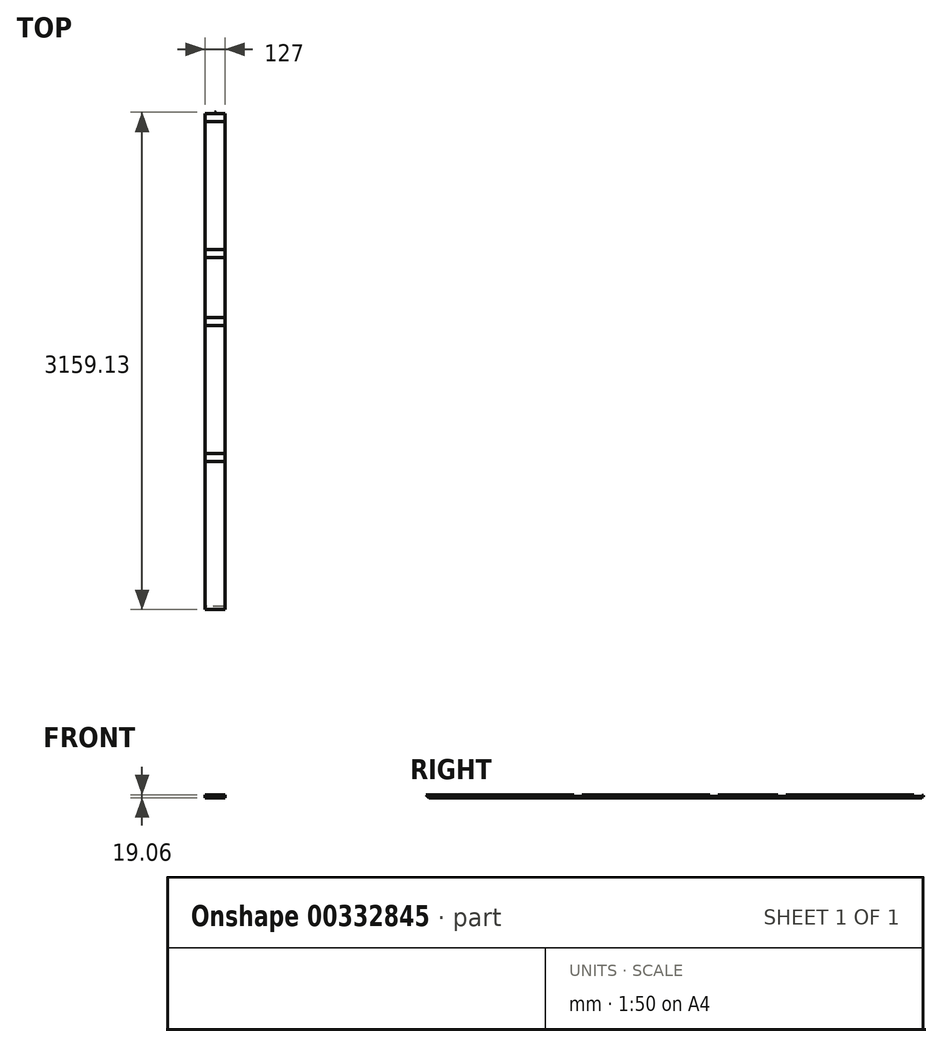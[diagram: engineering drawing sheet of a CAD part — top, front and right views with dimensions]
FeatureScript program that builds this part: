
annotation { "Feature Type Name" : "Feature", "Feature Type Description" : "" }
export const myFeature = defineFeature(function(context is Context, id is Id, definition is map)
    precondition{}
    {
        {
            var Q0;
            Q0=qCreatedBy(makeId("Right.planeOp"),FACE);
            var sketch = newSketch(context, id + "F0", { "sketchPlane" : qUnion([Q0])});
            skLineSegment(sketch, "E0.top", {"start": v(2997.2, -9.52) * mm, "end": v(2997.2, 0) * mm});
            skLineSegment(sketch, "E0.right", {"start": v(0, 9.52) * mm, "end": v(787.4, 9.53) * mm});
            skLineSegment(sketch, "E1.top", {"start": v(2946.4, 9.53) * mm, "end": v(2946.4, 0) * mm});
            skLineSegment(sketch, "E1.right", {"start": v(2997.2, 0) * mm, "end": v(2946.4, 0) * mm});
            skLineSegment(sketch, "E2", {"start": v(2997.2, -9.52) * mm, "end": v(-33.3, -9.53) * mm});
            skLineSegment(sketch, "E3.bottom", {"start": v(2133.6, 9.53) * mm, "end": v(2133.6, 0) * mm});
            skLineSegment(sketch, "E3.top", {"start": v(2082.8, 9.53) * mm, "end": v(2082.8, 0) * mm});
            skLineSegment(sketch, "E3.right", {"start": v(2133.6, 0) * mm, "end": v(2082.8, 0) * mm});
            skLineSegment(sketch, "E4.trimOffspring", {"start": v(2133.6, 9.53) * mm, "end": v(2946.4, 9.53) * mm});
            skLineSegment(sketch, "E5.top", {"start": v(1651, 9.53) * mm, "end": v(1651, 0) * mm});
            skLineSegment(sketch, "E5.right", {"start": v(1701.8, 0) * mm, "end": v(1651, 0) * mm});
            skLineSegment(sketch, "E6.bottom", {"start": v(838.2, 9.53) * mm, "end": v(838.2, 0) * mm});
            skLineSegment(sketch, "E6.top", {"start": v(787.4, 9.53) * mm, "end": v(787.4, 0) * mm});
            skLineSegment(sketch, "E6.right", {"start": v(838.2, 0) * mm, "end": v(787.4, 0) * mm});
            skPoint(sketch, "E6.left.start.orphan", {"position": v(838.2, 48.5) * mm});
            skPoint(sketch, "E7.orphan", {"position": v(787.4, 48.5) * mm});
            skLineSegment(sketch, "E8.trimOffspring", {"start": v(838.2, 9.53) * mm, "end": v(1651, 9.53) * mm});
            skLineSegment(sketch, "E9", {"start": v(1701.8, 0) * mm, "end": v(1701.8, 9.53) * mm});
            skLineSegment(sketch, "E10.trimOffspring", {"start": v(1701.8, 9.53) * mm, "end": v(2082.8, 9.53) * mm});
            skLineSegment(sketch, "E11", {"start": v(0, 9.52) * mm, "end": v(-152.4, 9.52) * mm});
            skLineSegment(sketch, "E12", {"start": v(-152.4, 9.52) * mm, "end": v(-133.35, -9.53) * mm});
            skLineSegment(sketch, "E13", {"start": v(-33.3, -9.53) * mm, "end": v(-133.35, -9.53) * mm});
            skPoint(sketch, "E14.start.orphan", {"position": v(431.8, 9.53) * mm});
            skSolve(sketch);
        }
        {
            var Q0;
            Q0=qSketchRegion(id+"F0",true);
            extrude(context, id + "F1", {"entities" : qUnion([Q0]), "endBound" : BoundingType.SYMMETRIC, "depth" : 127 * mm});
        }
        {
            var Q0;
            Q0=qCreatedBy(makeId("Front.planeOp"),FACE);
            cPlane(context, id + "F2", {"entities" : qUnion([Q0]), "cplaneType" : CPlaneType.OFFSET, "offset" : 2997.2 * mm, "oppositeDirection" : true, "width" : 152.4 * mm, "height" : 152.4 * mm});
        }
        {
            var Q0;
            Q0=qCreatedBy(id+"F2.planeOp",FACE);
            var sketch = newSketch(context, id + "F3", { "sketchPlane" : qUnion([Q0])});
            skCircle(sketch, "E15", {"center": v(0, 0) * mm, "radius": 4.76 * mm});
            skSolve(sketch);
        }
        {
            var Q0;
            Q0=qSketchRegion(id+"F3",true);
            extrude(context, id + "F4", {"entities" : qUnion([Q0]), "operationType" : NewBodyOperationType.ADD, "oppositeDirection" : true, "depth" : 9.52 * mm});
        }
    });
